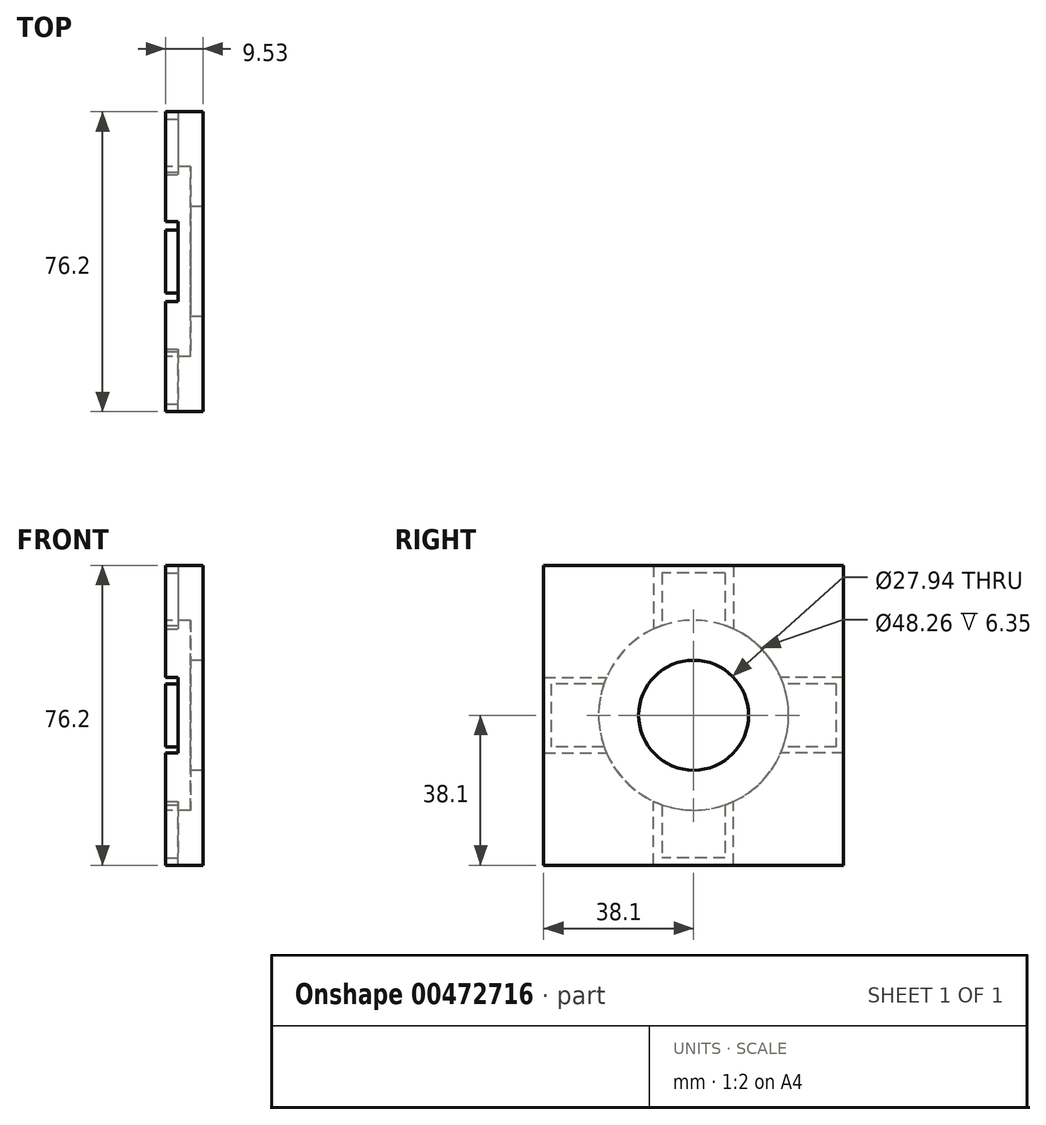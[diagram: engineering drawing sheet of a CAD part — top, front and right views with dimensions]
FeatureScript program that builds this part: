
annotation { "Feature Type Name" : "Feature", "Feature Type Description" : "" }
export const myFeature = defineFeature(function(context is Context, id is Id, definition is map)
    precondition{}
    {
        {
            var Q0;
            Q0=qCreatedBy(makeId("Right.planeOp"),FACE);
            var sketch = newSketch(context, id + "F0", { "sketchPlane" : qUnion([Q0])});
            skLineSegment(sketch, "E0.bottom", {"start": v(38.1, 38.1) * mm, "end": v(-38.1, 38.1) * mm});
            skLineSegment(sketch, "E0.top", {"start": v(38.1, -38.1) * mm, "end": v(-38.1, -38.1) * mm});
            skLineSegment(sketch, "E0.left", {"start": v(-38.1, -38.1) * mm, "end": v(-38.1, 38.1) * mm});
            skLineSegment(sketch, "E0.right", {"start": v(38.1, -38.1) * mm, "end": v(38.1, 38.1) * mm});
            skPoint(sketch, "E0.middle", {"position": v(0, 0) * mm});
            skCircle(sketch, "E1", {"center": v(0, 0) * mm, "radius": 24.13 * mm});
            skCircle(sketch, "E2.0", {"center": v(0, 0) * mm, "radius": 13.97 * mm});
            skSolve(sketch);
        }
        {
            var Q0;
            Q0=makeQuery(id+"F0.imprint","IMPRINT",FACE,{"disambiguationData":[TD([[makeQuery(id+"F0.imprint","IMPRINT",EDGE,{"derivedFrom":sQuery(id+"F0.wireOp",EDGE,"E0.bottom")}),1.0]])]});
            var Q1;
            Q1=makeQuery(id+"F0.imprint","IMPRINT",FACE,{"disambiguationData":[TD([[makeQuery(id+"F0.imprint","IMPRINT",EDGE,{"derivedFrom":sQuery(id+"F0.wireOp",EDGE,"E1")}),1.0]])]});
            var Q2;
            Q2=makeQuery(id+"F0.imprint","IMPRINT",FACE,{"disambiguationData":[TD([[makeQuery(id+"F0.imprint","IMPRINT",EDGE,{"derivedFrom":sQuery(id+"F0.wireOp",EDGE,"E2.0")}),-1.0]])]});
            extrude(context, id + "F1", {"entities" : qUnion([Q0, Q1, Q2]), "depth" : 6.35 * mm});
        }
        {
            var Q0;
            Q0=makeQuery(id+"F0.imprint","IMPRINT",FACE,{"disambiguationData":[TD([[makeQuery(id+"F0.imprint","IMPRINT",EDGE,{"derivedFrom":sQuery(id+"F0.wireOp",EDGE,"E1")}),1.0]])]});
            extrude(context, id + "F3", {"entities" : qUnion([Q0]), "operationType" : NewBodyOperationType.REMOVE, "depth" : 3.17 * mm});
        }
        {
            var Q0;
            Q0=makeQuery(id+"F0.imprint","IMPRINT",FACE,{"disambiguationData":[TD([[makeQuery(id+"F0.imprint","IMPRINT",EDGE,{"derivedFrom":sQuery(id+"F0.wireOp",EDGE,"E0.bottom")}),1.0]])]});
            var sketch = newSketch(context, id + "F4", { "sketchPlane" : qUnion([Q0])});
            skLineSegment(sketch, "E3.0", {"start": v(38.1, 38.1) * mm, "end": v(-38.1, 38.1) * mm});
            skLineSegment(sketch, "E3.1", {"start": v(38.1, -38.1) * mm, "end": v(38.1, 38.1) * mm});
            skLineSegment(sketch, "E3.2", {"start": v(38.1, -38.1) * mm, "end": v(10.16, -38.1) * mm});
            skLineSegment(sketch, "E3.3", {"start": v(-38.1, -38.1) * mm, "end": v(-38.1, -9.59) * mm});
            skArc(sketch, "E3.4", {"start": v(10.16, -21.89) * mm, "mid": v(17.28, -16.84) * mm, "end": v(22.14, -9.59) * mm});
            skLineSegment(sketch, "E4.bottom", {"start": v(38.1, 38.1) * mm, "end": v(10.16, 38.1) * mm});
            skLineSegment(sketch, "E4.top", {"start": v(38.1, 9.59) * mm, "end": v(22.14, 9.59) * mm});
            skLineSegment(sketch, "E4.left", {"start": v(38.1, 38.1) * mm, "end": v(38.1, 9.59) * mm});
            skLineSegment(sketch, "E4.right", {"start": v(10.16, 38.1) * mm, "end": v(10.16, 21.89) * mm});
            skLineSegment(sketch, "E5.bottom", {"start": v(-38.1, 38.1) * mm, "end": v(-10.16, 38.1) * mm});
            skLineSegment(sketch, "E5.top", {"start": v(-38.1, 9.59) * mm, "end": v(-22.14, 9.59) * mm});
            skLineSegment(sketch, "E5.left", {"start": v(-38.1, 38.1) * mm, "end": v(-38.1, 9.59) * mm});
            skLineSegment(sketch, "E5.right", {"start": v(-10.16, 38.1) * mm, "end": v(-10.16, 21.89) * mm});
            skLineSegment(sketch, "E6.top", {"start": v(38.1, -9.59) * mm, "end": v(22.14, -9.59) * mm});
            skLineSegment(sketch, "E6.left", {"start": v(38.1, -38.1) * mm, "end": v(38.1, -9.59) * mm});
            skLineSegment(sketch, "E6.right", {"start": v(10.16, -38.1) * mm, "end": v(10.16, -21.89) * mm});
            skLineSegment(sketch, "E7.bottom", {"start": v(-38.1, -38.1) * mm, "end": v(-10.16, -38.1) * mm});
            skLineSegment(sketch, "E7.top", {"start": v(-38.1, -9.59) * mm, "end": v(-22.14, -9.59) * mm});
            skLineSegment(sketch, "E7.right", {"start": v(-10.16, -38.1) * mm, "end": v(-10.16, -21.89) * mm});
            skLineSegment(sketch, "E8.bottom", {"start": v(36.2, 8) * mm, "end": v(22.76, 8) * mm});
            skLineSegment(sketch, "E8.top", {"start": v(36.2, -8) * mm, "end": v(22.76, -8) * mm});
            skLineSegment(sketch, "E8.left", {"start": v(36.2, 8) * mm, "end": v(36.2, -8) * mm});
            skLineSegment(sketch, "E8.right", {"start": v(-36.2, 8) * mm, "end": v(-36.2, -8) * mm});
            skLineSegment(sketch, "E9.bottom", {"start": v(8, 36.2) * mm, "end": v(-8, 36.2) * mm});
            skLineSegment(sketch, "E9.top", {"start": v(8, -36.2) * mm, "end": v(-8, -36.2) * mm});
            skLineSegment(sketch, "E9.left", {"start": v(8, 36.2) * mm, "end": v(8, 22.76) * mm});
            skLineSegment(sketch, "E9.right", {"start": v(-8, 36.2) * mm, "end": v(-8, 22.76) * mm});
            skLineSegment(sketch, "E10.trimOffspring", {"start": v(-22.76, 8) * mm, "end": v(-36.2, 8) * mm});
            skLineSegment(sketch, "E11.trimOffspring", {"start": v(-22.76, -8) * mm, "end": v(-36.2, -8) * mm});
            skLineSegment(sketch, "E12.trimOffspring", {"start": v(-8, -22.76) * mm, "end": v(-8, -36.2) * mm});
            skLineSegment(sketch, "E13.trimOffspring", {"start": v(8, -22.76) * mm, "end": v(8, -36.2) * mm});
            skLineSegment(sketch, "E14.trimOffspring", {"start": v(-38.1, 9.59) * mm, "end": v(-38.1, 38.1) * mm});
            skLineSegment(sketch, "E15.trimOffspring", {"start": v(-10.16, -38.1) * mm, "end": v(-38.1, -38.1) * mm});
            skArc(sketch, "E16.trimOffspring", {"start": v(-8, -22.76) * mm, "mid": v(0, -24.13) * mm, "end": v(8, -22.76) * mm});
            skArc(sketch, "E17.trimOffspring", {"start": v(22.14, 9.59) * mm, "mid": v(17.28, 16.84) * mm, "end": v(10.16, 21.89) * mm});
            skArc(sketch, "E18.trimOffspring", {"start": v(22.76, -8) * mm, "mid": v(24.13, 0) * mm, "end": v(22.76, 8) * mm});
            skArc(sketch, "E19.trimOffspring", {"start": v(8, 22.76) * mm, "mid": v(0, 24.13) * mm, "end": v(-8, 22.76) * mm});
            skArc(sketch, "E20.trimOffspring", {"start": v(-10.16, 21.89) * mm, "mid": v(-17.28, 16.84) * mm, "end": v(-22.14, 9.59) * mm});
            skArc(sketch, "E21.trimOffspring", {"start": v(-22.76, 8) * mm, "mid": v(-24.13, 0) * mm, "end": v(-22.76, -8) * mm});
            skArc(sketch, "E22.trimOffspring", {"start": v(-22.14, -9.59) * mm, "mid": v(-17.28, -16.84) * mm, "end": v(-10.16, -21.89) * mm});
            skSolve(sketch);
        }
        {
            var Q0;
            Q0=qSketchRegion(id+"F4",true);
            extrude(context, id + "F5", {"entities" : qUnion([Q0]), "operationType" : NewBodyOperationType.ADD, "oppositeDirection" : true, "depth" : 3.17 * mm});
        }
    });
